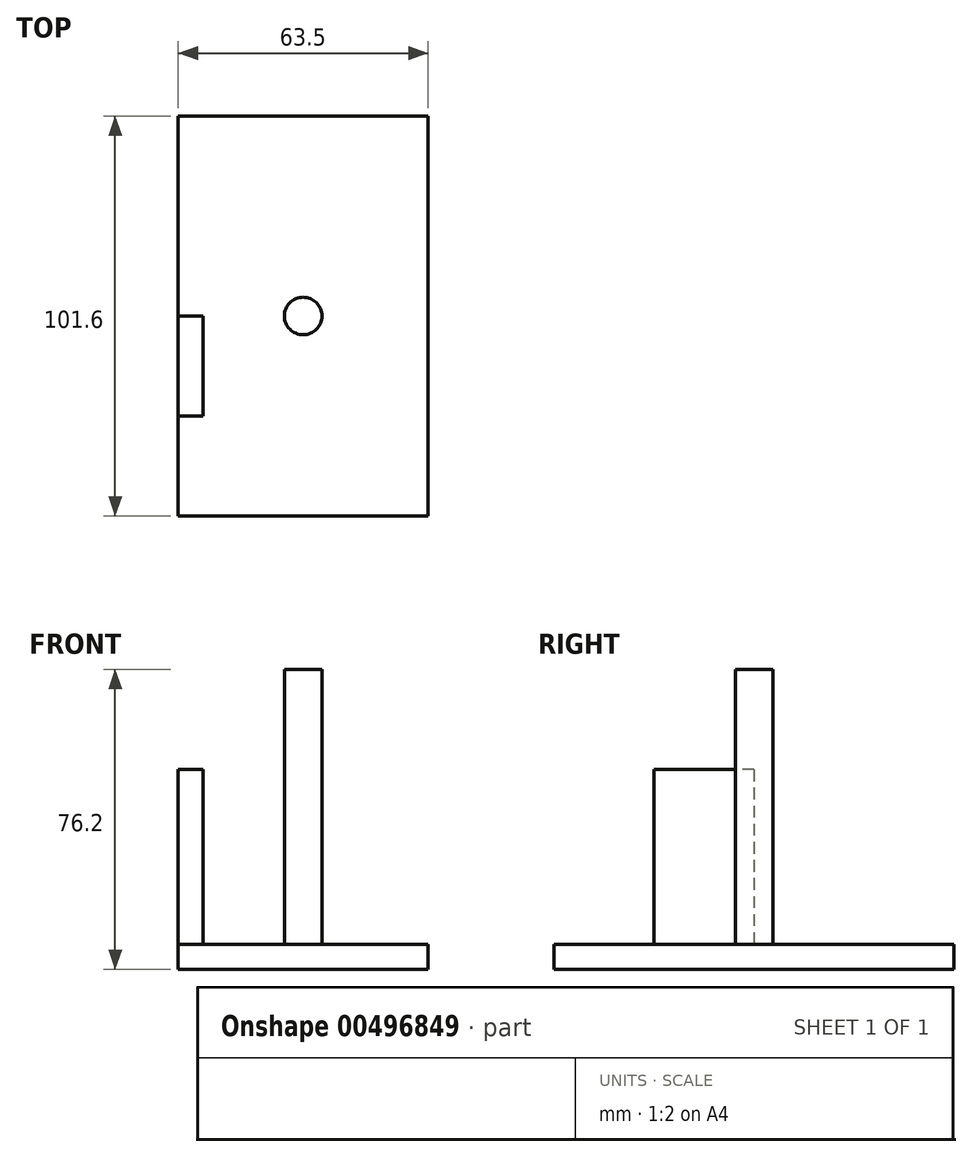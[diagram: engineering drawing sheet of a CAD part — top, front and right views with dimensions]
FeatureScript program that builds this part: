
annotation { "Feature Type Name" : "Feature", "Feature Type Description" : "" }
export const myFeature = defineFeature(function(context is Context, id is Id, definition is map)
    precondition{}
    {
        {
            var Q0;
            Q0=qCreatedBy(makeId("Top.planeOp"),FACE);
            var sketch = newSketch(context, id + "F0", { "sketchPlane" : qUnion([Q0])});
            skPoint(sketch, "E0.0", {"position": v(0, 0) * mm});
            skLineSegment(sketch, "E1.bottom", {"start": v(-31.75, 50.8) * mm, "end": v(31.75, 50.8) * mm});
            skLineSegment(sketch, "E1.top", {"start": v(-31.75, -50.8) * mm, "end": v(31.75, -50.8) * mm});
            skLineSegment(sketch, "E1.left", {"start": v(-31.75, 50.8) * mm, "end": v(-31.75, -50.8) * mm});
            skLineSegment(sketch, "E1.right", {"start": v(31.75, 50.8) * mm, "end": v(31.75, -50.8) * mm});
            skSolve(sketch);
        }
        {
            var Q0;
            Q0=makeQuery(id+"F0.imprint","IMPRINT",FACE,{"disambiguationData":[TD([[makeQuery(id+"F0.imprint","IMPRINT",EDGE,{"derivedFrom":sQuery(id+"F0.wireOp",EDGE,"E1.bottom")}),-1.0]])]});
            extrude(context, id + "F1", {"entities" : qUnion([Q0]), "depth" : 6.35 * mm});
        }
        {
            var Q0;
            Q0=makeQuery(id+"F1.opExtrude","CAP_FACE",FACE,{"disambiguationData":[OSD([sQuery(id+"F0.wireOp",EDGE,"E1.bottom"),sQuery(id+"F0.wireOp",EDGE,"E1.top"),sQuery(id+"F0.wireOp",EDGE,"E1.left"),sQuery(id+"F0.wireOp",EDGE,"E1.right")])],"isStart":false});
            var sketch = newSketch(context, id + "F2", { "sketchPlane" : qUnion([Q0])});
            skPoint(sketch, "E2.0", {"position": v(0, 0) * mm});
            skCircle(sketch, "E3", {"center": v(0, 0) * mm, "radius": 4.76 * mm});
            skSolve(sketch);
        }
        {
            var Q0;
            Q0=makeQuery(id+"F2.imprint","IMPRINT",FACE,{"disambiguationData":[TD([[makeQuery(id+"F2.imprint","IMPRINT",EDGE,{"derivedFrom":sQuery(id+"F2.wireOp",EDGE,"E3")}),1.0]])]});
            extrude(context, id + "F3", {"entities" : qUnion([Q0]), "operationType" : NewBodyOperationType.ADD, "depth" : 69.85 * mm});
        }
        {
            var Q0;
            Q0=makeQuery(id+"F1.opExtrude","CAP_FACE",FACE,{"disambiguationData":[OSD([sQuery(id+"F0.wireOp",EDGE,"E1.bottom"),sQuery(id+"F0.wireOp",EDGE,"E1.top"),sQuery(id+"F0.wireOp",EDGE,"E1.left"),sQuery(id+"F0.wireOp",EDGE,"E1.right")])],"isStart":false});
            var sketch = newSketch(context, id + "F4", { "sketchPlane" : qUnion([Q0])});
            skPoint(sketch, "E4.0", {"position": v(-31.75, 0) * mm});
            skLineSegment(sketch, "E5.0.0", {"start": v(-31.75, 50.8) * mm, "end": v(-31.75, -50.8) * mm});
            skLineSegment(sketch, "E5.0.1", {"start": v(-31.75, -50.8) * mm, "end": v(31.75, -50.8) * mm});
            skLineSegment(sketch, "E5.0.2", {"start": v(31.75, -50.8) * mm, "end": v(31.75, 50.8) * mm});
            skLineSegment(sketch, "E5.0.3", {"start": v(31.75, 50.8) * mm, "end": v(-31.75, 50.8) * mm});
            skLineSegment(sketch, "E6.bottom", {"start": v(-31.75, 0) * mm, "end": v(-25.4, 0) * mm});
            skLineSegment(sketch, "E6.top", {"start": v(-31.75, -25.4) * mm, "end": v(-25.4, -25.4) * mm});
            skLineSegment(sketch, "E6.left", {"start": v(-31.75, 0) * mm, "end": v(-31.75, -25.4) * mm});
            skLineSegment(sketch, "E6.right", {"start": v(-25.4, 0) * mm, "end": v(-25.4, -25.4) * mm});
            skSolve(sketch);
        }
        {
            var Q0;
            Q0=makeQuery(id+"F4.imprint","IMPRINT",FACE,{"disambiguationData":[TD([[makeQuery(id+"F4.imprint","IMPRINT",EDGE,{"derivedFrom":sQuery(id+"F4.wireOp",EDGE,"E6.bottom")}),-1.0]])]});
            extrude(context, id + "F5", {"entities" : qUnion([Q0]), "operationType" : NewBodyOperationType.ADD, "depth" : 44.45 * mm});
        }
    });
